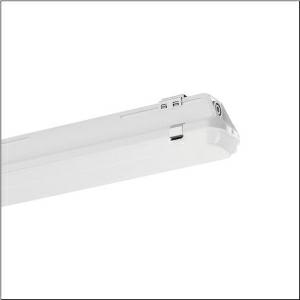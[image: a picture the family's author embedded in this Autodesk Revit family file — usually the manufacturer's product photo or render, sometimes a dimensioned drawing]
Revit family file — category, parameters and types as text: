
# Revit family: monsun_11_emergency_51fp10dp467l3h
name_source: partatom
category: Lighting Fixtures
units: mm (PartAtom-declared; Revit-internal decimal feet)

## family parameters
Cut with Voids When Loaded = No
Host = Face
Light Source = No
Part Type = Normal
Room Calculation Point = No
Round Connector Dimension = Use Diameter
Shared = No

## types (1)
- --- (1 x LED, 1010 lm, 6.2 W, 4000K)
    Apparent Load = 6 VA
    CIE Flux Codes = 47 77 93 94 100
    Color Rendering = 80
    Color Temperature = 4000K
    Default Elevation = 1800 mm
    Description = Monsun 11 emergency, damp-proof luminaire, chain hanger, primary optical cover: enclosure, of PMMA, light emission: direct distribution, primary light characteristic: symmetric, installation type: suspended mounting, surface-mounted, horizontal mounting, vertical mounting, LED, rated luminous flux: 6.050lm, luminous efficacy: 192lm/W, light colour: 840, colour temperature: 4000K, control gear: DALI 2, with terminal, 5+3-pole, max. 2.5mm², mains connection: 220..240V, AC, 50/60Hz, rated input power: 35W, control gear: single battery element, battery: LiFePO4, 9Ah, luminaire housing, of glass-fibre reinforced polyester, uncoated, bright grey, incl. chain hanger, length: 1.590mm, width: 90mm, height: 88mm, clip for enclosure, of stainless steel (V2A), ceiling mounting element, of stainless steel (V2A), chain hanger, of stainless steel (V2A), protection rating (complete): IP66, insulation class (complete): insulation class I (protective earthing), certification: CE, UKCA, protection symbol: D, impact resistance: IK04, permissible operating ambient temperature: +5..+35°C, standard: EN 50419, EN 60598-2-1, EN 60598-2-22, corresponds to IFS (International Featured Standards) requirements for safety and quality in the food industry, for indoor or canopied outdoor use, no direct snow, no direct sun, no direct rain, LABS conformity tested according to VDMA 24364:2018-05, contact your sales advisor before using the luminaires in applications with unclear chemical exposure, large temperature fluctuations or condensation-forming humidity, packaging unit: 1 piece
    Height = 89 mm
    Lamp = 1 x LED
    Lamp Light Flux = 1010 lm
    Lamp Power = 6.2 W
    Lamp count = 1
    Length = 1590 mm
    Luminous efficacy = 163 lm/W
    Manufacturer = Siteco
    ModVariant = No
    Model = 51FP10DP467L3H
    Mounting Place = Ceiling
    Mounting Type = Surface mounted
    Number of Poles = 1
    OnlyDefault = Yes
    Power Factor = 1
    Product Name = Monsun 11 emergency
    Product group = damp-proof luminaire
    ProductGroupID = 300
    Protection Class = Protection class I
    Protection Degree = IP 66
    RLX_Detail_Level = 1
    RLX_Emergency_Light_Flux = 0 lm
    RLX_Emergency_Type = 0
    RLX_Emergency_Type_DB = No
    RlxData = <blob elided: 92421 chars, md5=bd7957f1>
    Socket = socket
    Standby Power = 0 W
    System Light Flux = 1010 lm
    System Power = 6 W
    Type Comments = : emergency light operation: 3 h
    Type Image = l_1349237.jpg
    URL = http://relux.com
    VarID = @adj_033897
    Voltage = 0 V
    Weight = 0.00 kg
    Width = 90 mm

## geometry (parser evidence)
native form markers: Blend x4, Sweep x14
no freeform markers — native parametric forms only
